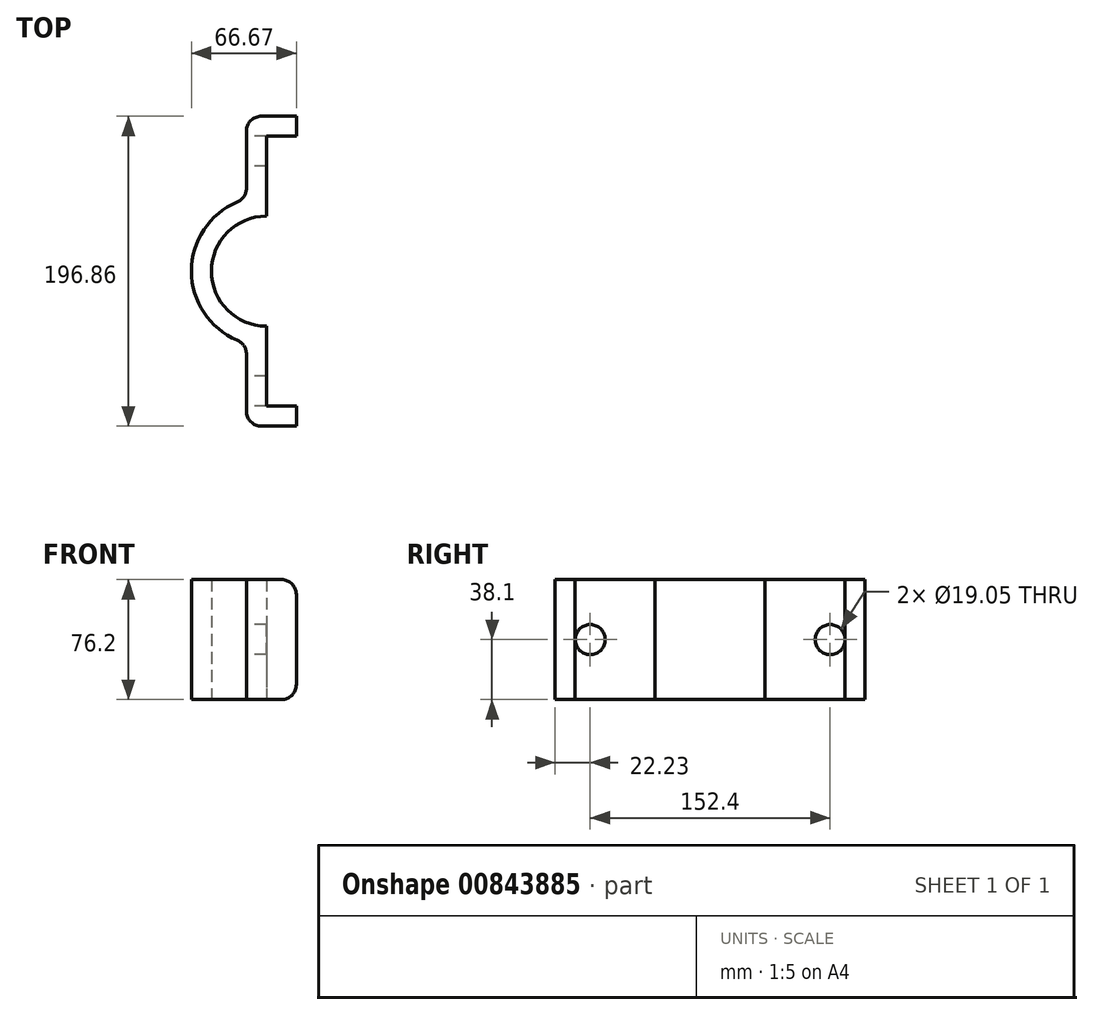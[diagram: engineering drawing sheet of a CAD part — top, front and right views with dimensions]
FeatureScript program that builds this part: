
annotation { "Feature Type Name" : "Feature", "Feature Type Description" : "" }
export const myFeature = defineFeature(function(context is Context, id is Id, definition is map)
    precondition{}
    {
        {
            var Q0;
            Q0=qCreatedBy(makeId("Top.planeOp"),FACE);
            var sketch = newSketch(context, id + "F0", { "sketchPlane" : qUnion([Q0])});
            skArc(sketch, "E0", {"start": v(0, 34.93) * mm, "mid": v(-34.93, 0) * mm, "end": v(0, -34.93) * mm});
            skArc(sketch, "E1", {"start": v(-12.7, 45.9) * mm, "mid": v(-47.63, 0) * mm, "end": v(-12.7, -45.9) * mm});
            skLineSegment(sketch, "E2", {"start": v(0, 85.73) * mm, "end": v(0, 56.88) * mm});
            skLineSegment(sketch, "E3", {"start": v(-12.7, 45.9) * mm, "end": v(-12.7, 98.43) * mm});
            skLineSegment(sketch, "E4", {"start": v(0, -85.73) * mm, "end": v(19.05, -85.73) * mm});
            skLineSegment(sketch, "E5", {"start": v(19.05, -85.73) * mm, "end": v(19.05, -98.43) * mm});
            skLineSegment(sketch, "E6", {"start": v(19.05, -98.43) * mm, "end": v(-12.7, -98.43) * mm});
            skLineSegment(sketch, "E7", {"start": v(-12.7, 98.43) * mm, "end": v(19.05, 98.43) * mm});
            skLineSegment(sketch, "E8", {"start": v(19.05, 98.43) * mm, "end": v(19.05, 85.73) * mm});
            skLineSegment(sketch, "E9", {"start": v(19.05, 85.73) * mm, "end": v(0, 85.73) * mm});
            skLineSegment(sketch, "E10.trimOffspring", {"start": v(0, 85.73) * mm, "end": v(0, 47.63) * mm});
            skPoint(sketch, "E11.orphan", {"position": v(-12.7, -99.73) * mm});
            skPoint(sketch, "E12.orphan", {"position": v(0, -98.43) * mm});
            skLineSegment(sketch, "E13.trimOffspring", {"start": v(-12.7, -45.9) * mm, "end": v(-12.7, -98.43) * mm});
            skLineSegment(sketch, "E14.trimOffspring", {"start": v(0, -47.63) * mm, "end": v(0, -85.73) * mm});
            skLineSegment(sketch, "E15", {"start": v(0, 47.63) * mm, "end": v(0, 34.93) * mm});
            skLineSegment(sketch, "E16.trimOffspring", {"start": v(0, -34.93) * mm, "end": v(0, -47.63) * mm});
            skSolve(sketch);
        }
        {
            var Q0;
            Q0=makeQuery(id+"F0.imprint","IMPRINT",FACE,{"disambiguationData":[TD([[makeQuery(id+"F0.imprint","IMPRINT",EDGE,{"derivedFrom":sQuery(id+"F0.wireOp",EDGE,"E0")}),-1.0]])]});
            extrude(context, id + "F1", {"entities" : qUnion([Q0]), "depth" : 76.2 * mm, "offsetDistance" : 25.4 * mm});
        }
        {
            var Q0;
            Q0=makeQuery(id+"F1.opExtrude","SWEPT_FACE",FACE,{"disambiguationData":[OSD([sQuery(id+"F0.wireOp",EDGE,"E13.trimOffspring")])]});
            var sketch = newSketch(context, id + "F2", { "sketchPlane" : qUnion([Q0])});
            skCircle(sketch, "E17", {"center": v(76.2, 38.1) * mm, "radius": 9.53 * mm});
            skCircle(sketch, "E18", {"center": v(-76.2, 38.1) * mm, "radius": 9.53 * mm});
            skSolve(sketch);
        }
        {
            var Q0;
            Q0=makeQuery(id+"F2.imprint","IMPRINT",FACE,{"disambiguationData":[TD([[makeQuery(id+"F2.imprint","IMPRINT",EDGE,{"derivedFrom":sQuery(id+"F2.wireOp",EDGE,"E18")}),1.0]])]});
            var Q1;
            Q1=makeQuery(id+"F2.imprint","IMPRINT",FACE,{"disambiguationData":[TD([[makeQuery(id+"F2.imprint","IMPRINT",EDGE,{"derivedFrom":sQuery(id+"F2.wireOp",EDGE,"E17")}),1.0]])]});
            extrude(context, id + "F3", {"entities" : qUnion([Q0, Q1]), "operationType" : NewBodyOperationType.REMOVE, "oppositeDirection" : true, "depth" : 25.4 * mm, "offsetDistance" : 25.4 * mm});
        }
        {
            var Q0;
            Q0=makeQuery(id+"F1.opExtrude","SWEPT_EDGE",EDGE,{"disambiguationData":[OSD([sQuery(id+"F0.wireOp",EDGE,"E1"),sQuery(id+"F0.wireOp",EDGE,"E13.trimOffspring")])]});
            var Q1;
            Q1=makeQuery(id+"F1.opExtrude","SWEPT_EDGE",EDGE,{"disambiguationData":[OSD([sQuery(id+"F0.wireOp",EDGE,"E1"),sQuery(id+"F0.wireOp",EDGE,"E3")])]});
            var Q2;
            Q2=makeQuery(id+"F1.opExtrude","SWEPT_EDGE",EDGE,{"disambiguationData":[OSD([sQuery(id+"F0.wireOp",EDGE,"E3"),sQuery(id+"F0.wireOp",EDGE,"E7")])]});
            var Q3;
            Q3=makeQuery(id+"F1.opExtrude","SWEPT_EDGE",EDGE,{"disambiguationData":[OSD([sQuery(id+"F0.wireOp",EDGE,"E6"),sQuery(id+"F0.wireOp",EDGE,"E13.trimOffspring")])]});
            var Q4;
            Q4=makeQuery(id+"F1.opExtrude","CAP_EDGE",EDGE,{"disambiguationData":[OSD([sQuery(id+"F0.wireOp",EDGE,"E5")])],"isStart":true});
            var Q5;
            Q5=makeQuery(id+"F1.opExtrude","CAP_EDGE",EDGE,{"disambiguationData":[OSD([sQuery(id+"F0.wireOp",EDGE,"E8")])],"isStart":true});
            var Q6;
            Q6=makeQuery(id+"F1.opExtrude","CAP_EDGE",EDGE,{"disambiguationData":[OSD([sQuery(id+"F0.wireOp",EDGE,"E8")])],"isStart":false});
            var Q7;
            Q7=makeQuery(id+"F1.opExtrude","CAP_EDGE",EDGE,{"disambiguationData":[OSD([sQuery(id+"F0.wireOp",EDGE,"E5")])],"isStart":false});
            fillet(context, id + "F4", {"entities" : qUnion([Q0, Q1, Q2, Q3, Q4, Q5, Q6, Q7]), "radius" : 9.52 * mm, "tangentPropagation" : true, "allowEdgeOverflow" : false});
        }
    });
